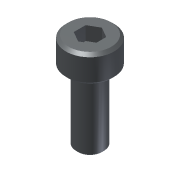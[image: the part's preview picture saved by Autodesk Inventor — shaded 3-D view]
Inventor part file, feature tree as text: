
AUTODESK INVENTOR PART (.ipt)
format: ipt  version: 2013 (Build 170138000, 138)  size: 93,184 bytes
history: native  units: in
note: dims shown in document units (in); Inventor stores cm internally (conversion verified against a paired STEP export)
features: chamfer x1, other x1, imported_body x1
ambient origin geometry x8: Origin, YZ Plane, XZ Plane, XY Plane, X Axis, Y Axis, Z Axis, Center Point
feature tree (3):
  chamfer  "Chamfer2"  [1 undecoded]
  other  "SSA_SSAM4-0010ZC1"
  imported_body  "Base1"
note: 1 required parameter value undecoded (feature->parameter linkage not recoverable at this tier; creation-order binding heuristic only, values carry confidence <= 0.55)
